# Revit family: Sanitary_Accessories_hansgrohe_26844700-Rainfinity-Shelf-500-26844700_new
name_source: partatom
category: Furniture
revit_build: Autodesk Revit 2015 (Build: 20140903_1530(x64)
units: mm (PartAtom-declared; Revit-internal decimal feet)

## types (1)
- Matt White
    BIMobject category = Accessories
    BIMobject category code = sanitary-accessories1
    BIMobject main category = Sanitary
    BIMobject main category code = sanitary
    BOSUseNativeGeometries = 1
    Brand url = http://www.hansgrohe-int.com
    Default Elevation = 4' - 0"
    Edition number = 1
    IFC Classification = Sanitary Terminal
    Installation instructions = https://pro.hansgrohe-int.com
    Manufacturer country = Germany
    Manufacturer name = hansgrohe
    NBS Reference Code = 31-75
    NBS Reference Description = Sanitary Accessories
    Product Guid = e53a9831-d88d-4956-a1f8-e8e1db9f310d
    Product SKU = 26844700
    Product data url = https://bimobject.com
    Product family = Rainfinity
    Product group = Accessories
    Product name = 26844700 Rainfinity Shelf 500 26844700
    Product url = https://pro.hansgrohe-int.com
    QR code = http://bimobject.com
    Technical description = https://pro.hansgrohe-int.com
    UNSPSC Code = 301815
    Uniclass 1.4 Code = L721
    Uniclass 1.4 Description = Sanitary equipment
    Uniclass 2.0 Code = PR-31-75
    Uniclass 2.0 Description = Sanitary Accessories
    Uniclass 2015 Code = Pr_40_20_76
    Uniclass 2015 Name = Sanitary accessories
    Uniformat II Code = D2090
    Uniformat II Description = Other Plumbing Systems

## geometry (parser evidence)
native form markers: Sweep x3
no freeform markers — native parametric forms only
